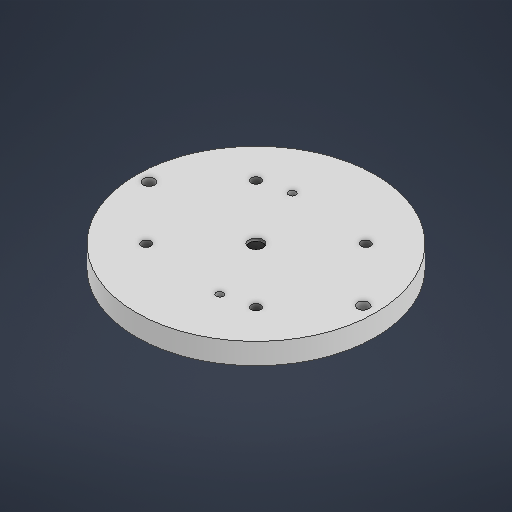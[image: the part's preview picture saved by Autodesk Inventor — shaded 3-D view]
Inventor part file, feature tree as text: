
AUTODESK INVENTOR PART (.ipt)
format: ipt  version: 2025 (Build 290162000, 162)  size: 263,680 bytes
history: native  units: in
note: dims shown in document units (in); Inventor stores cm internally (conversion verified against a paired STEP export)
features: sketch x8, hole x4, extrude x3
ambient origin geometry x8: Origin, YZ Plane, XZ Plane, XY Plane, X Axis, Y Axis, Z Axis, Center Point
bodies: Solid1 (feature_tree)
feature tree (15):
  extrude  "Extrusion1"  Depth=0.5906in TaperAngle=0.0deg
  sketch  "Sketch2"  dims[d5=0.315in d6=0.1772in]
  extrude  "Extrusion2"  Depth=0.315in
  extrude  "Extrusion3"  Depth=0.1772in
  hole  "Hole1"  [1 undecoded]
  hole  "Hole2"  [1 undecoded]
  hole  "Hole3"  [1 undecoded]
  hole  "Hole4"  [1 undecoded]
  sketch  "Sketch1"  dims[d0=6.6732in d1=0.5906in d2=0.0in]
  sketch  "Sketch3"  dims[d10=0.4724in d11=0.0in d12=1.5748in]
  sketch  "Sketch Circular Pattern1"  dims[d3=5.9843in d4=0.315in]
  sketch  "Sketch4"  dims[d13=0.315in d14=1.5748in d16=360.0deg]
  sketch  "Sketch Circular Pattern2"  dims[d7=0.1772in d8=0.0in d9=0.0in]
  sketch  "Sketch5"  dims[d21=4.3307in d22=4.3307in]
  sketch  "Sketch6"  dims[d23=4.3307in d24=0.315in d25=0.315in d26=0.315in d27=0.315in d28=0.2617in d29=0.7874in d30=0.1575in d31=0.0787in d32=90.0deg d33=0.7874in d34=0.8108in d35=3.7402in d36=0.1969in d37=6.2992in d39=360.0deg d41=0.1969in d42=0.4724in d43=0.1575in d44=0.0787in d45=90.0deg d46=0.4724in d47=0.8108in d48=0.3979in d49=0.9449in d50=0.8268in d51=0.5118in d52=90.0deg d53=1.2717in d54=0.8108in d55=0.2617in d56=0.7874in d57=0.748in d58=0.3543in d59=90.0deg d60=0.7874in d61=0.8108in]
note: 4 required parameter values undecoded (feature->parameter linkage not recoverable at this tier; creation-order binding heuristic only, values carry confidence <= 0.55)
